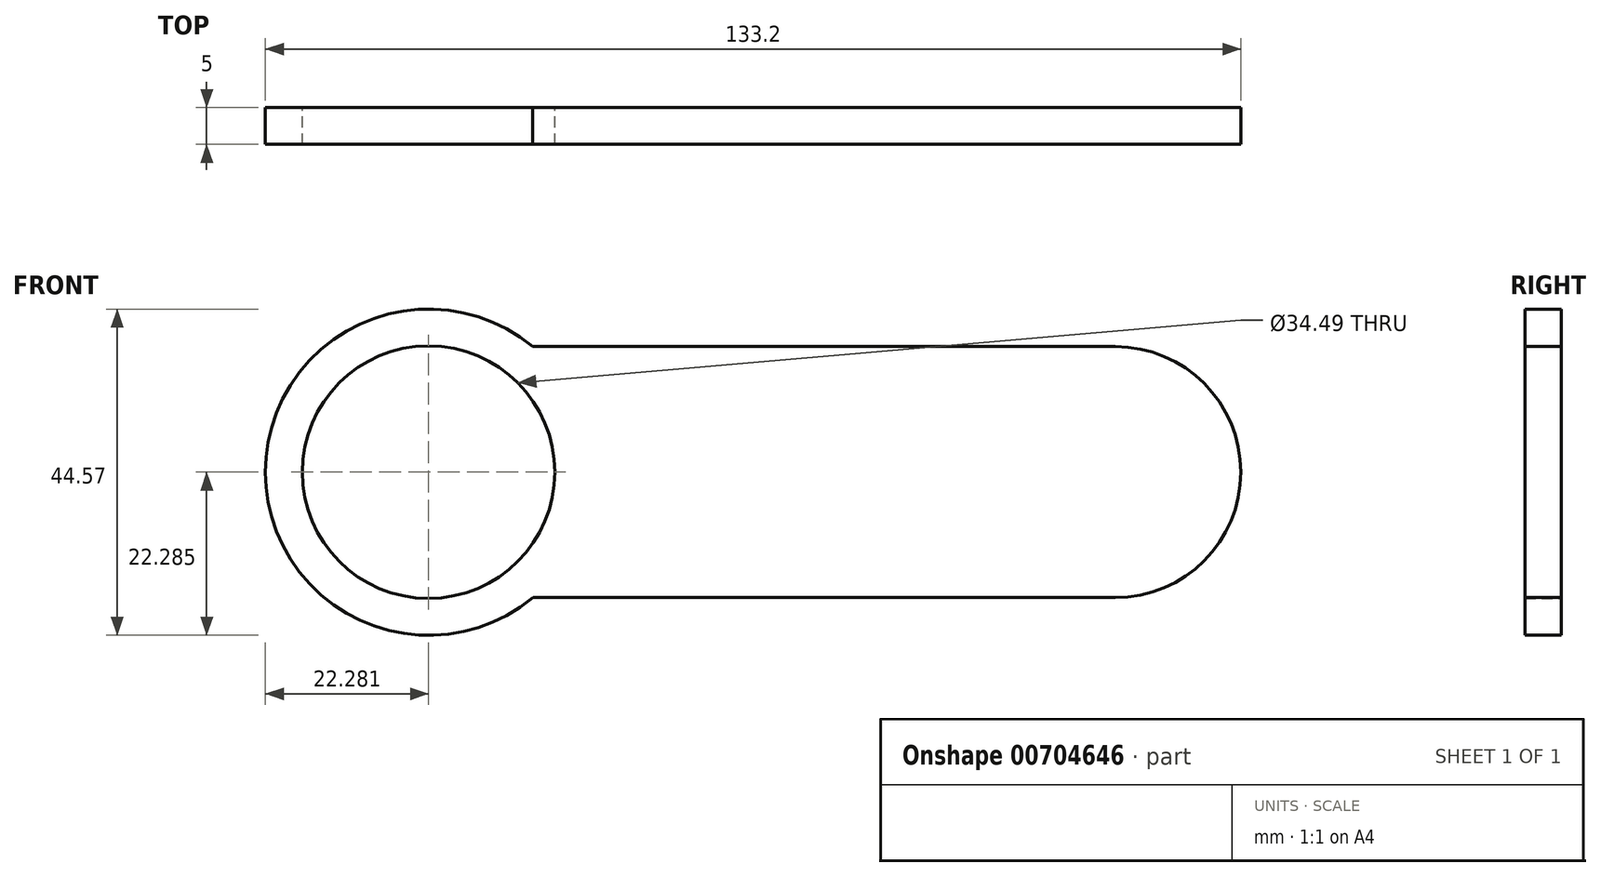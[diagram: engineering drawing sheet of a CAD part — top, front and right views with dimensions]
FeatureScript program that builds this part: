
annotation { "Feature Type Name" : "Feature", "Feature Type Description" : "" }
export const myFeature = defineFeature(function(context is Context, id is Id, definition is map)
    precondition{}
    {
        {
            var Q0;
            Q0=qCreatedBy(makeId("Front.planeOp"),FACE);
            var sketch = newSketch(context, id + "F0", { "sketchPlane" : qUnion([Q0])});
            skLineSegment(sketch, "E0", {"start": v(-55.1, -25.54) * mm, "end": v(37.96, -25.54) * mm});
            skLineSegment(sketch, "E1", {"start": v(-55.8, 8.75) * mm, "end": v(37.96, 8.75) * mm});
            skArc(sketch, "E2", {"start": v(37.96, -25.54) * mm, "mid": v(55.1, -8.4) * mm, "end": v(37.96, 8.75) * mm});
            skArc(sketch, "E3", {"start": v(-55.8, 8.75) * mm, "mid": v(-72.96, -8.75) * mm, "end": v(-55.1, -25.54) * mm});
            skArc(sketch, "E4", {"start": v(-55.8, 8.75) * mm, "mid": v(-38.66, -8.05) * mm, "end": v(-55.1, -25.54) * mm});
            skCircle(sketch, "E5", {"center": v(-55.8, -8.4) * mm, "radius": 17.25 * mm});
            skCircle(sketch, "E6", {"center": v(-55.8, -8.4) * mm, "radius": 22.28 * mm});
            skPoint(sketch, "E7.startSnap0", {"position": v(-38.66, -8.05) * mm});
            skPoint(sketch, "E8.startSnap0", {"position": v(-72.96, -8.75) * mm});
            skArc(sketch, "E9", {"start": v(37.96, -17.84) * mm, "mid": v(44.76, -8.92) * mm, "end": v(37.96, 0) * mm});
            skLineSegment(sketch, "E10", {"start": v(37.96, 0) * mm, "end": v(37.96, 2.5) * mm});
            skLineSegment(sketch, "E11", {"start": v(37.96, -17.84) * mm, "end": v(37.96, -20.34) * mm});
            skArc(sketch, "E12", {"start": v(37.96, -20.34) * mm, "mid": v(48.23, -8.92) * mm, "end": v(37.96, 2.5) * mm});
            skSolve(sketch);
        }
        {
            var Q0;
            Q0 = qSketchRegion(id + "F0", true);
            var Q1;
            Q1=makeQuery(id+"F0.imprint","IMPRINT",FACE,{"disambiguationData":[TD([[makeQuery(id+"F0.imprint","IMPRINT",EDGE,{"derivedFrom":sQuery(id+"F0.wireOp",EDGE,"E9")}),-1.0]])]});
            extrude(context, id + "F1", {"entities" : qUnion([Q0, Q1]), "depth" : 5 * mm, "offsetDistance" : 25.4 * mm});
        }
        {
            var Q0;
            Q0=sQuery(id+"F0.wireOp",EDGE,"E6");
            extrude(context, id + "F2", {"bodyType" : ToolBodyType.SURFACE, "surfaceEntities" : qUnion([Q0]), "depth" : 60 * mm, "offsetDistance" : 25 * mm});
        }
        {
            var Q0;
            Q0=sQuery(id+"F0.wireOp",EDGE,"E12");
            var Q1;
            Q1=sQuery(id+"F0.wireOp",EDGE,"E9");
            var Q2;
            Q2=sQuery(id+"F0.wireOp",EDGE,"E10");
            var Q3;
            Q3=sQuery(id+"F0.wireOp",EDGE,"E11");
            extrude(context, id + "F3", {"bodyType" : ToolBodyType.SURFACE, "surfaceEntities" : qUnion([Q0, Q1, Q2, Q3]), "depth" : 10 * mm, "offsetDistance" : 25 * mm});
        }
    });
